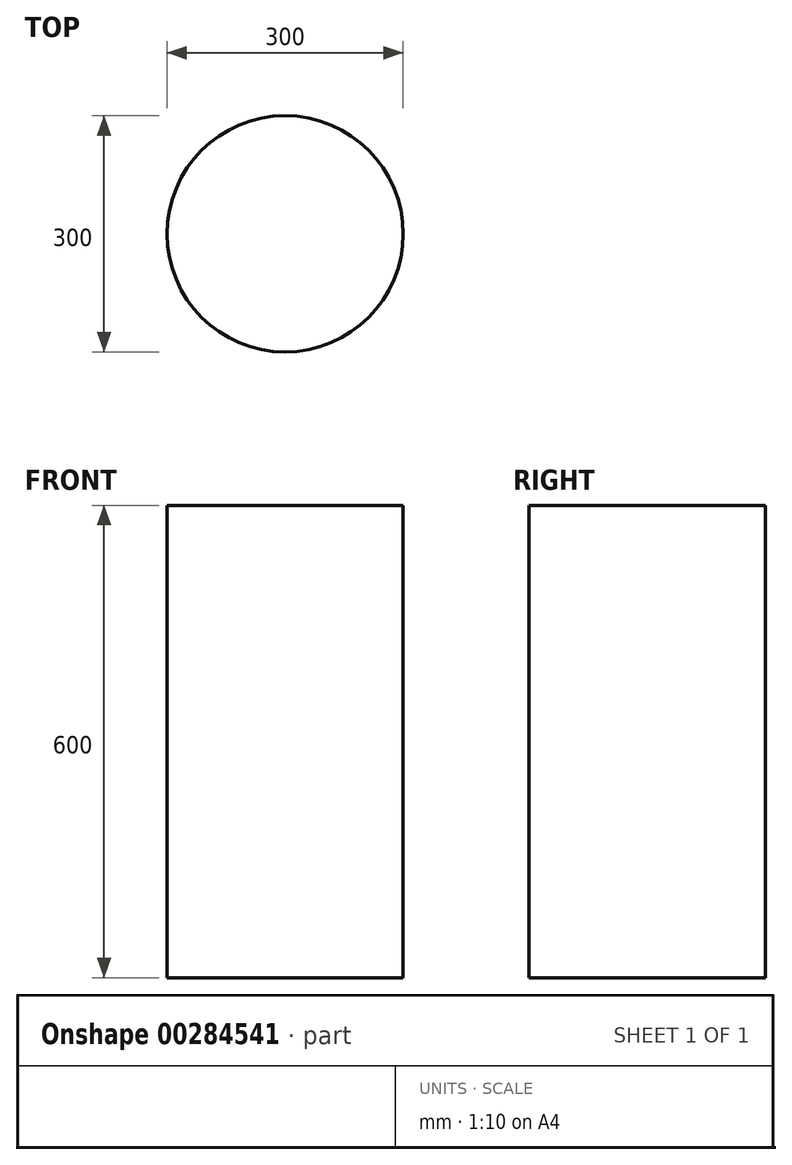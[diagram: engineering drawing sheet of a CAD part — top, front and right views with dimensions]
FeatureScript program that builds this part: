
annotation { "Feature Type Name" : "Feature", "Feature Type Description" : "" }
export const myFeature = defineFeature(function(context is Context, id is Id, definition is map)
    precondition{}
    {
        {
            var Q0;
            Q0=qCreatedBy(makeId("Top.planeOp"),FACE);
            var sketch = newSketch(context, id + "F0", { "sketchPlane" : qUnion([Q0])});
            skCircle(sketch, "E0", {"center": v(0, 0) * mm, "radius": 150 * mm});
            skSolve(sketch);
        }
        {
            var Q0;
            Q0=makeQuery(id+"F0.imprint","IMPRINT",FACE,{"disambiguationData":[TD([[makeQuery(id+"F0.imprint","IMPRINT",EDGE,{"derivedFrom":sQuery(id+"F0.wireOp",EDGE,"E0")}),1.0]])]});
            extrude(context, id + "F1", {"entities" : qUnion([Q0]), "depth" : 600 * mm});
        }
    });
